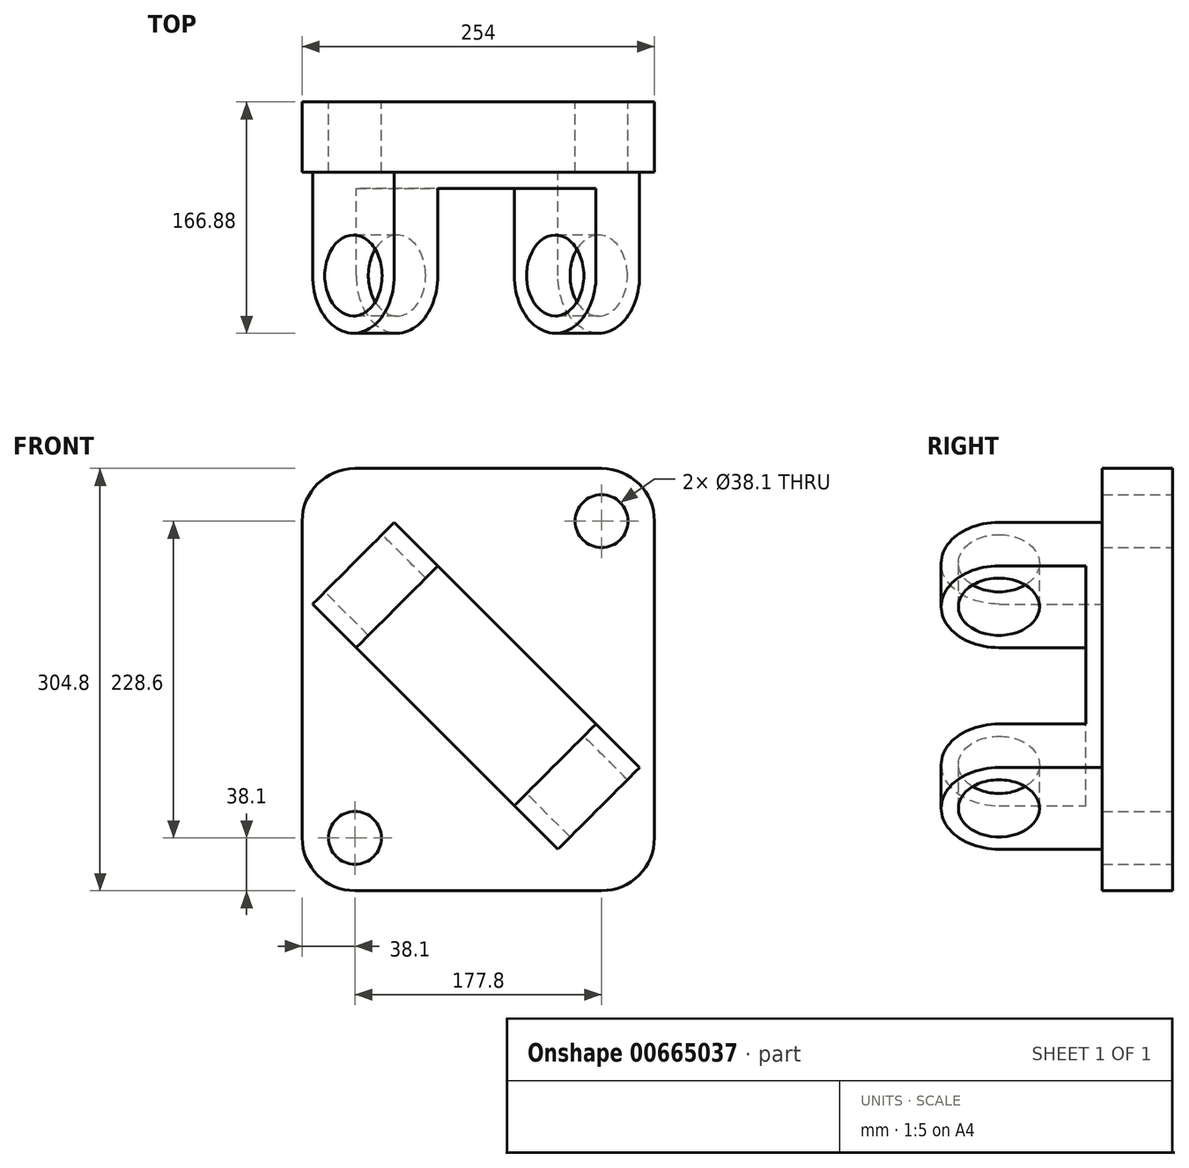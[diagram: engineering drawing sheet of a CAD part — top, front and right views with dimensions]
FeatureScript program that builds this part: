
annotation { "Feature Type Name" : "Feature", "Feature Type Description" : "" }
export const myFeature = defineFeature(function(context is Context, id is Id, definition is map)
    precondition{}
    {
        {
            var Q0;
            Q0=qCreatedBy(makeId("Front.planeOp"),FACE);
            var sketch = newSketch(context, id + "F0", { "sketchPlane" : qUnion([Q0])});
            skLineSegment(sketch, "E0", {"start": v(38.1, 0) * mm, "end": v(215.9, 0) * mm});
            skLineSegment(sketch, "E1", {"start": v(254, 38.1) * mm, "end": v(254, 266.7) * mm});
            skLineSegment(sketch, "E2", {"start": v(215.9, 304.8) * mm, "end": v(38.1, 304.8) * mm});
            skLineSegment(sketch, "E3", {"start": v(0, 266.7) * mm, "end": v(0, 38.1) * mm});
            skPoint(sketch, "E4.visualSharp", {"position": v(0, 304.8) * mm});
            skArc(sketch, "E4.filletArc", {"start": v(38.1, 304.8) * mm, "mid": v(11.16, 293.64) * mm, "end": v(0, 266.7) * mm});
            skPoint(sketch, "E5.visualSharp", {"position": v(254, 304.8) * mm});
            skArc(sketch, "E5.filletArc", {"start": v(254, 266.7) * mm, "mid": v(242.84, 293.64) * mm, "end": v(215.9, 304.8) * mm});
            skPoint(sketch, "E6.visualSharp", {"position": v(254, 0) * mm});
            skArc(sketch, "E6.filletArc", {"start": v(215.9, 0) * mm, "mid": v(242.84, 11.16) * mm, "end": v(254, 38.1) * mm});
            skPoint(sketch, "E7.visualSharp", {"position": v(0, 0) * mm});
            skArc(sketch, "E7.filletArc", {"start": v(0, 38.1) * mm, "mid": v(11.16, 11.16) * mm, "end": v(38.1, 0) * mm});
            skCircle(sketch, "E8", {"center": v(38.1, 38.1) * mm, "radius": 19.05 * mm});
            skCircle(sketch, "E9", {"center": v(215.9, 266.7) * mm, "radius": 19.05 * mm});
            skLineSegment(sketch, "E10", {"start": v(184.4, 29.97) * mm, "end": v(7.5, 206.88) * mm});
            skLineSegment(sketch, "E11.0", {"start": v(243.31, 88.88) * mm, "end": v(66.4, 265.8) * mm});
            skLineSegment(sketch, "E12", {"start": v(184.4, 29.97) * mm, "end": v(243.31, 88.88) * mm});
            skLineSegment(sketch, "E13", {"start": v(7.5, 206.88) * mm, "end": v(66.4, 265.8) * mm});
            skLineSegment(sketch, "E14.0", {"start": v(152.97, 61.4) * mm, "end": v(211.88, 120.31) * mm});
            skLineSegment(sketch, "E15.0", {"start": v(38.92, 175.45) * mm, "end": v(97.83, 234.36) * mm});
            skSolve(sketch);
        }
        {
            var Q0;
            Q0=makeQuery(id+"F0.imprint","IMPRINT",FACE,{"disambiguationData":[TD([[makeQuery(id+"F0.imprint","IMPRINT",EDGE,{"derivedFrom":sQuery(id+"F0.wireOp",EDGE,"E0")}),1.0]])]});
            extrude(context, id + "F1", {"entities" : qUnion([Q0]), "depth" : 50.8 * mm, "offsetDistance" : 25.4 * mm});
        }
        {
            var Q0;
            {var subQ0=sQuery(id+"F0.wireOp",EDGE,"E14.0");Q0=makeQuery(id+"F0.imprint","IMPRINT",FACE,{"disambiguationData":[TD([[makeQuery(id+"F0.imprint","IMPRINT",EDGE,{"derivedFrom":subQ0}),1.0]])]});}
            extrude(context, id + "F2", {"entities" : qUnion([Q0]), "operationType" : NewBodyOperationType.ADD, "depth" : 62.48 * mm, "offsetDistance" : 25.4 * mm});
        }
        {
            var Q0;
            {var subQ0=sQuery(id+"F0.wireOp",EDGE,"E12");Q0=makeQuery(id+"F0.imprint","IMPRINT",FACE,{"disambiguationData":[TD([[makeQuery(id+"F0.imprint","IMPRINT",EDGE,{"derivedFrom":subQ0}),1.0]])]});}
            var Q1;
            {var subQ0=sQuery(id+"F0.wireOp",EDGE,"E13");Q1=makeQuery(id+"F0.imprint","IMPRINT",FACE,{"disambiguationData":[TD([[makeQuery(id+"F0.imprint","IMPRINT",EDGE,{"derivedFrom":subQ0}),-1.0]])]});}
            extrude(context, id + "F3", {"entities" : qUnion([Q0, Q1]), "operationType" : NewBodyOperationType.ADD, "depth" : 125.22 * mm, "offsetDistance" : 25.4 * mm});
        }
        {
            var Q0;
            Q0=makeQuery(id+"F3.opExtrude","SWEPT_FACE",FACE,{"disambiguationData":[OSD([sQuery(id+"F0.wireOp",EDGE,"E12")])]});
            var sketch = newSketch(context, id + "F4", { "sketchPlane" : qUnion([Q0])});
            skArc(sketch, "E16", {"start": v(-125.22, 234.9) * mm, "mid": v(-166.88, 193.24) * mm, "end": v(-125.22, 151.59) * mm});
            skSolve(sketch);
        }
        {
            var Q0;
            Q0=makeQuery(id+"F4.imprint","IMPRINT",FACE,{"disambiguationData":[TD([[makeQuery(id+"F4.imprint","IMPRINT",EDGE,{"derivedFrom":sQuery(id+"F4.wireOp",EDGE,"E16")}),1.0]])]});
            extrude(context, id + "F5", {"entities" : qUnion([Q0]), "operationType" : NewBodyOperationType.ADD, "oppositeDirection" : true, "depth" : 44.45 * mm, "offsetDistance" : 25.4 * mm});
        }
        {
            var Q0;
            Q0=makeQuery(id+"F3.opExtrude","SWEPT_FACE",FACE,{"disambiguationData":[OSD([sQuery(id+"F0.wireOp",EDGE,"E13")])]});
            var sketch = newSketch(context, id + "F6", { "sketchPlane" : qUnion([Q0])});
            skArc(sketch, "E17", {"start": v(125.22, 151.59) * mm, "mid": v(166.88, 193.24) * mm, "end": v(125.22, 234.9) * mm});
            skCircle(sketch, "E18", {"center": v(125.22, 193.24) * mm, "radius": 29.21 * mm});
            skSolve(sketch);
        }
        {
            var Q0;
            Q0=makeQuery(id+"F6.imprint","IMPRINT",FACE,{"disambiguationData":[TD([[makeQuery(id+"F6.imprint","IMPRINT",EDGE,{"derivedFrom":sQuery(id+"F6.wireOp",EDGE,"E17")}),1.0]])]});
            extrude(context, id + "F7", {"entities" : qUnion([Q0]), "operationType" : NewBodyOperationType.ADD, "oppositeDirection" : true, "depth" : 44.45 * mm, "offsetDistance" : 25.4 * mm});
        }
        {
            var Q0;
            {var subQ0=sQuery(id+"F6.wireOp",EDGE,"E18");var subQ1=makeQuery(id+"F3.opExtrude","CAP_EDGE",EDGE,{"disambiguationData":[OSD([sQuery(id+"F0.wireOp",EDGE,"E13")])],"isStart":false});var subQ2=makeQuery(id+"F6.imprint","INTERSECT",VERTEX,{"disambiguationData":[OD(0.0)],"derivedFrom":[subQ1,subQ0]});Q0=makeQuery(id+"F6.imprint","IMPRINT",FACE,{"disambiguationData":[TD([[makeQuery(id+"F6.imprint","IMPRINT",EDGE,{"disambiguationData":[TD([[subQ2,-1.0]])],"derivedFrom":subQ0}),1.0]])]});}
            var Q1;
            {var subQ0=sQuery(id+"F6.wireOp",EDGE,"E18");var subQ1=makeQuery(id+"F3.opExtrude","CAP_EDGE",EDGE,{"disambiguationData":[OSD([sQuery(id+"F0.wireOp",EDGE,"E13")])],"isStart":false});var subQ2=makeQuery(id+"F6.imprint","INTERSECT",VERTEX,{"disambiguationData":[OD(0.0)],"derivedFrom":[subQ1,subQ0]});Q1=makeQuery(id+"F6.imprint","IMPRINT",FACE,{"disambiguationData":[TD([[makeQuery(id+"F6.imprint","IMPRINT",EDGE,{"disambiguationData":[TD([[subQ2,1.0]])],"derivedFrom":subQ0}),1.0]])]});}
            extrude(context, id + "F8", {"entities" : qUnion([Q0, Q1]), "operationType" : NewBodyOperationType.REMOVE, "oppositeDirection" : true, "depth" : 299.2 * mm, "offsetDistance" : 25.4 * mm});
        }
    });
